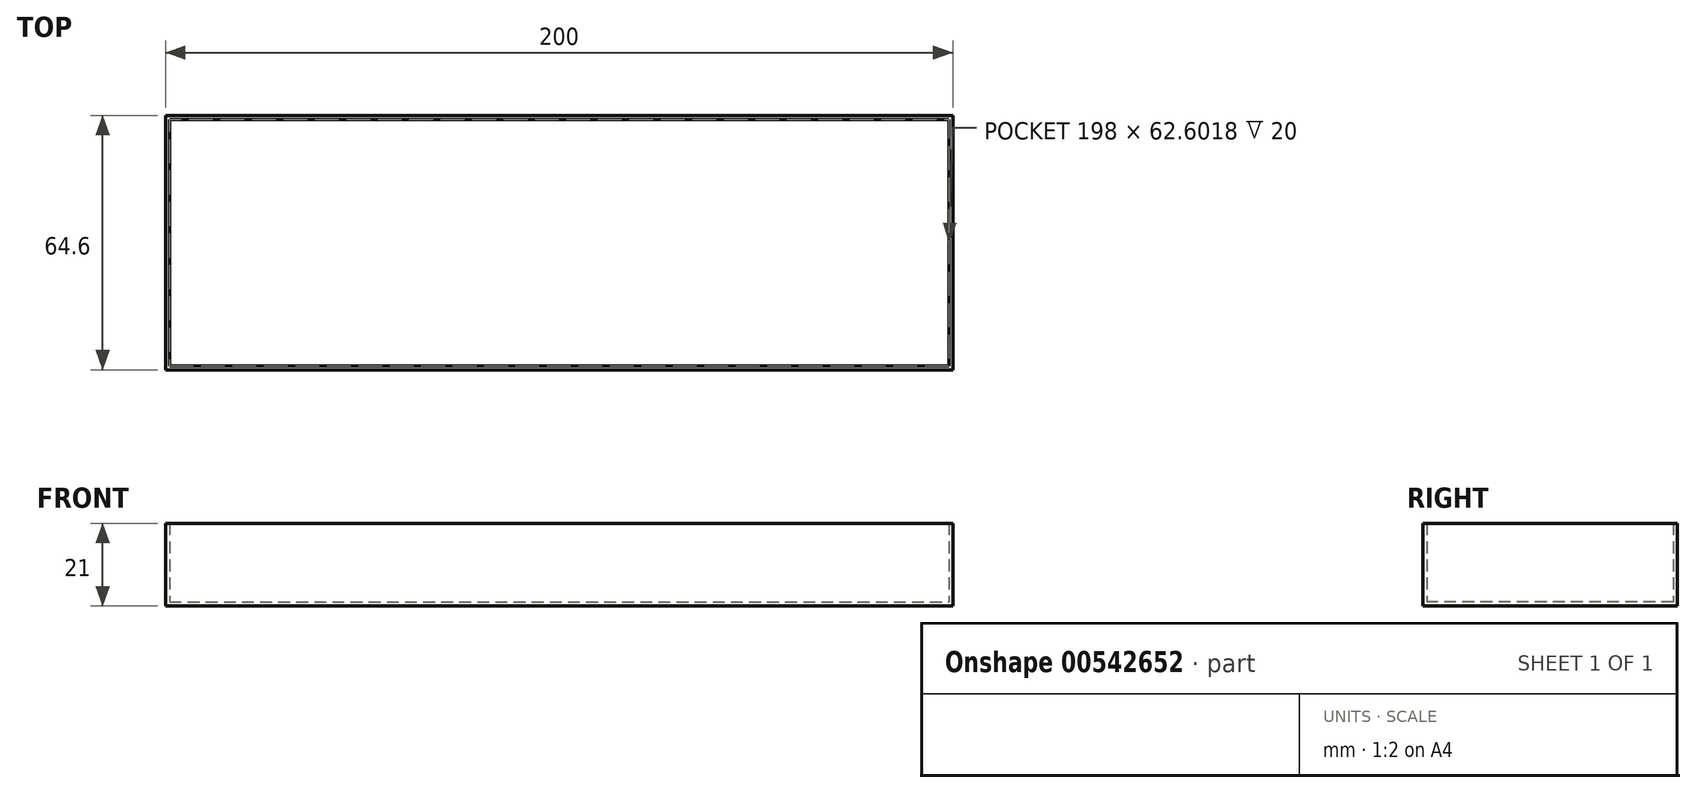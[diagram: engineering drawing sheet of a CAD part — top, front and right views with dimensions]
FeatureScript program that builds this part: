
annotation { "Feature Type Name" : "Feature", "Feature Type Description" : "" }
export const myFeature = defineFeature(function(context is Context, id is Id, definition is map)
    precondition{}
    {
        {
            var Q0;
            Q0=qCreatedBy(makeId("Top.planeOp"),FACE);
            var sketch = newSketch(context, id + "F0", { "sketchPlane" : qUnion([Q0])});
            skLineSegment(sketch, "E0.bottom", {"start": v(-100, 32.3) * mm, "end": v(100, 32.3) * mm});
            skLineSegment(sketch, "E0.top", {"start": v(-100, -32.3) * mm, "end": v(100, -32.3) * mm});
            skLineSegment(sketch, "E0.left", {"start": v(-100, 32.3) * mm, "end": v(-100, -32.3) * mm});
            skLineSegment(sketch, "E0.right", {"start": v(100, 32.3) * mm, "end": v(100, -32.3) * mm});
            skPoint(sketch, "E0.middle", {"position": v(0, 0) * mm});
            skSolve(sketch);
        }
        {
            var Q0;
            Q0 = qSketchRegion(id + "F0", true);
            extrude(context, id + "F1", {"entities" : qUnion([Q0]), "depth" : 1 * mm, "offsetDistance" : 25 * mm});
        }
        {
            var Q0;
            Q0=makeQuery(id+"F1.opExtrude","CAP_FACE",FACE,{"disambiguationData":[OSD([sQuery(id+"F0.wireOp",EDGE,"E0.bottom"),sQuery(id+"F0.wireOp",EDGE,"E0.top"),sQuery(id+"F0.wireOp",EDGE,"E0.left"),sQuery(id+"F0.wireOp",EDGE,"E0.right")])],"isStart":false});
            var sketch = newSketch(context, id + "F2", { "sketchPlane" : qUnion([Q0])});
            skLineSegment(sketch, "E1.bottom", {"start": v(-100, 32.3) * mm, "end": v(-99, 32.3) * mm});
            skLineSegment(sketch, "E1.top", {"start": v(-100, -32.3) * mm, "end": v(-99, -32.3) * mm});
            skLineSegment(sketch, "E1.left", {"start": v(-100, 32.3) * mm, "end": v(-100, -32.3) * mm});
            skLineSegment(sketch, "E1.right", {"start": v(-99, 32.3) * mm, "end": v(-99, -32.3) * mm});
            skSolve(sketch);
        }
        {
            var Q0;
            Q0 = qSketchRegion(id + "F2", true);
            extrude(context, id + "F3", {"entities" : qUnion([Q0]), "operationType" : NewBodyOperationType.ADD, "depth" : 20 * mm, "offsetDistance" : 25 * mm});
        }
        {
            var Q0;
            Q0=makeQuery(id+"F1.opExtrude","CAP_FACE",FACE,{"disambiguationData":[OSD([sQuery(id+"F0.wireOp",EDGE,"E0.bottom"),sQuery(id+"F0.wireOp",EDGE,"E0.top"),sQuery(id+"F0.wireOp",EDGE,"E0.left"),sQuery(id+"F0.wireOp",EDGE,"E0.right")])],"isStart":false});
            var sketch = newSketch(context, id + "F4", { "sketchPlane" : qUnion([Q0])});
            skLineSegment(sketch, "E2.bottom", {"start": v(-99, 32.3) * mm, "end": v(100, 32.3) * mm});
            skLineSegment(sketch, "E2.top", {"start": v(-99, 31.3) * mm, "end": v(100, 31.3) * mm});
            skLineSegment(sketch, "E2.left", {"start": v(-99, 32.3) * mm, "end": v(-99, 31.3) * mm});
            skLineSegment(sketch, "E2.right", {"start": v(100, 32.3) * mm, "end": v(100, 31.3) * mm});
            skSolve(sketch);
        }
        {
            var Q0;
            Q0 = qSketchRegion(id + "F4", true);
            extrude(context, id + "F5", {"entities" : qUnion([Q0]), "operationType" : NewBodyOperationType.ADD, "depth" : 20 * mm, "offsetDistance" : 25 * mm});
        }
        {
            var Q0;
            Q0=makeQuery(id+"F1.opExtrude","CAP_FACE",FACE,{"disambiguationData":[OSD([sQuery(id+"F0.wireOp",EDGE,"E0.bottom"),sQuery(id+"F0.wireOp",EDGE,"E0.top"),sQuery(id+"F0.wireOp",EDGE,"E0.left"),sQuery(id+"F0.wireOp",EDGE,"E0.right")])],"isStart":false});
            var sketch = newSketch(context, id + "F6", { "sketchPlane" : qUnion([Q0])});
            skLineSegment(sketch, "E3.bottom", {"start": v(-99, -32.3) * mm, "end": v(100, -32.3) * mm});
            skLineSegment(sketch, "E3.top", {"start": v(-99, -31.3) * mm, "end": v(100, -31.3) * mm});
            skLineSegment(sketch, "E3.left", {"start": v(-99, -32.3) * mm, "end": v(-99, -31.3) * mm});
            skLineSegment(sketch, "E3.right", {"start": v(100, -32.3) * mm, "end": v(100, -31.3) * mm});
            skSolve(sketch);
        }
        {
            var Q0;
            Q0 = qSketchRegion(id + "F6", true);
            extrude(context, id + "F7", {"entities" : qUnion([Q0]), "operationType" : NewBodyOperationType.ADD, "depth" : 20 * mm, "offsetDistance" : 25 * mm});
        }
        {
            var Q0;
            Q0=makeQuery(id+"F1.opExtrude","CAP_FACE",FACE,{"disambiguationData":[OSD([sQuery(id+"F0.wireOp",EDGE,"E0.bottom"),sQuery(id+"F0.wireOp",EDGE,"E0.top"),sQuery(id+"F0.wireOp",EDGE,"E0.left"),sQuery(id+"F0.wireOp",EDGE,"E0.right")])],"isStart":false});
            var sketch = newSketch(context, id + "F8", { "sketchPlane" : qUnion([Q0])});
            skLineSegment(sketch, "E4.bottom", {"start": v(100, 31.3) * mm, "end": v(99, 31.3) * mm});
            skLineSegment(sketch, "E4.top", {"start": v(100, -31.3) * mm, "end": v(99, -31.3) * mm});
            skLineSegment(sketch, "E4.left", {"start": v(100, 31.3) * mm, "end": v(100, -31.3) * mm});
            skLineSegment(sketch, "E4.right", {"start": v(99, 31.3) * mm, "end": v(99, -31.3) * mm});
            skSolve(sketch);
        }
        {
            var Q0;
            Q0 = qSketchRegion(id + "F8", true);
            extrude(context, id + "F9", {"entities" : qUnion([Q0]), "operationType" : NewBodyOperationType.ADD, "depth" : 20 * mm, "offsetDistance" : 25 * mm});
        }
    });
